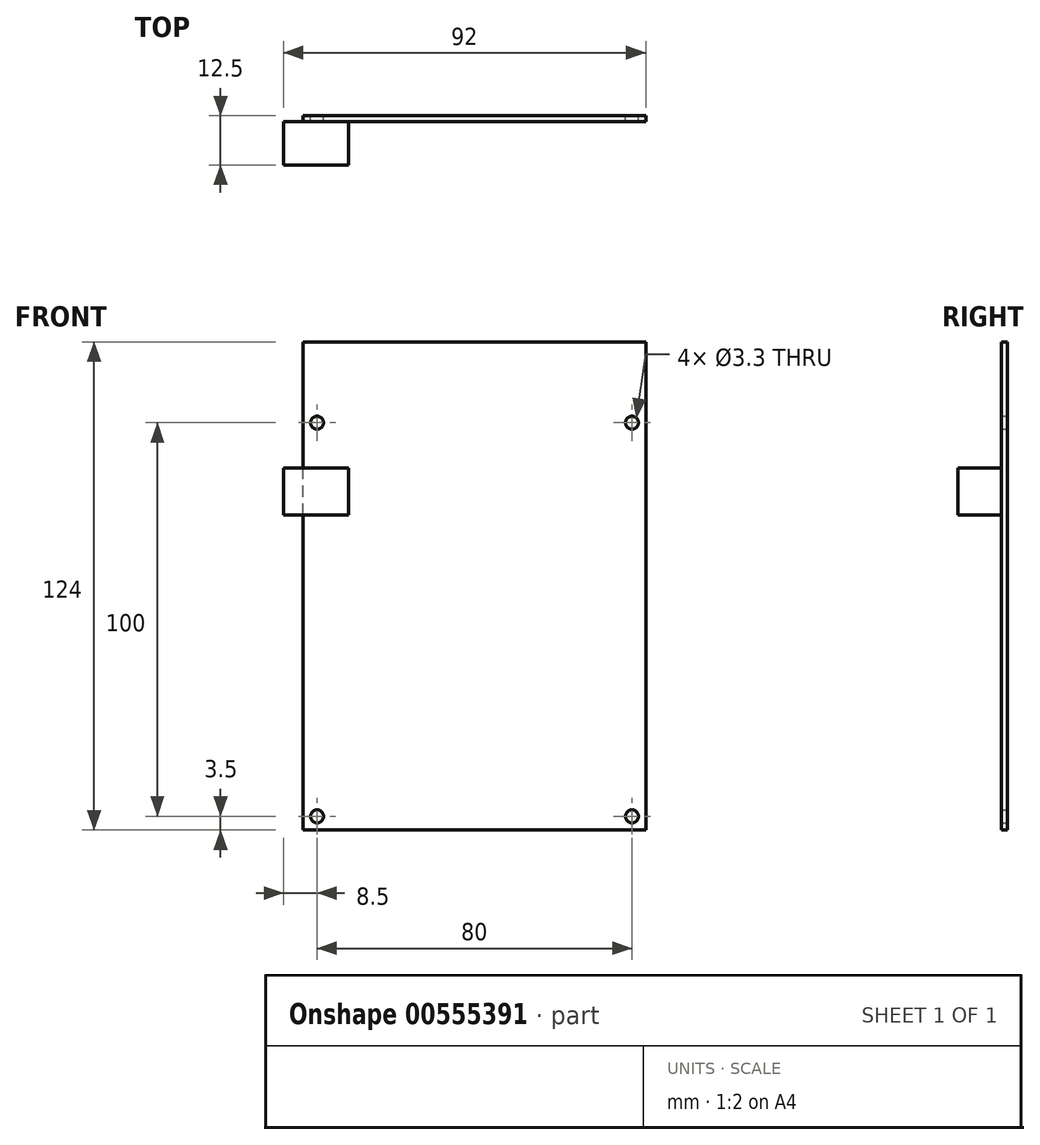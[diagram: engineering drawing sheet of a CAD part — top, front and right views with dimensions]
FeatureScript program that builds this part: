
annotation { "Feature Type Name" : "Feature", "Feature Type Description" : "" }
export const myFeature = defineFeature(function(context is Context, id is Id, definition is map)
    precondition{}
    {
        {
            var Q0;
            Q0=qCreatedBy(makeId("Front.planeOp"),FACE);
            var sketch = newSketch(context, id + "F0", { "sketchPlane" : qUnion([Q0])});
            skLineSegment(sketch, "E0.bottom", {"start": v(43.5, -62) * mm, "end": v(-43.5, -62) * mm});
            skLineSegment(sketch, "E0.top", {"start": v(43.5, 62) * mm, "end": v(-43.5, 62) * mm});
            skLineSegment(sketch, "E0.left", {"start": v(43.5, -62) * mm, "end": v(43.5, 62) * mm});
            skLineSegment(sketch, "E0.right", {"start": v(-43.5, -62) * mm, "end": v(-43.5, 62) * mm});
            skPoint(sketch, "E0.middle", {"position": v(0, 0) * mm});
            skCircle(sketch, "E1", {"center": v(-40, 41.5) * mm, "radius": 1.65 * mm});
            skCircle(sketch, "E2", {"center": v(-40, -58.5) * mm, "radius": 1.65 * mm});
            skCircle(sketch, "E3", {"center": v(40, 41.5) * mm, "radius": 1.65 * mm});
            skCircle(sketch, "E4", {"center": v(40, -58.5) * mm, "radius": 1.65 * mm});
            skLineSegment(sketch, "E5", {"start": v(0, 62) * mm, "end": v(0, -62) * mm, "construction": true});
            skSolve(sketch);
        }
        {
            var Q0;
            Q0=makeQuery(id+"F0.imprint","IMPRINT",FACE,{"disambiguationData":[TD([[makeQuery(id+"F0.imprint","IMPRINT",EDGE,{"derivedFrom":sQuery(id+"F0.wireOp",EDGE,"E0.bottom")}),-1.0]])]});
            extrude(context, id + "F1", {"entities" : qUnion([Q0]), "depth" : 1.5 * mm, "offsetDistance" : 25 * mm});
        }
        {
            var Q0;
            Q0=makeQuery(id+"F1.opExtrude","CAP_FACE",FACE,{"disambiguationData":[OSD([sQuery(id+"F0.wireOp",EDGE,"E0.bottom"),sQuery(id+"F0.wireOp",EDGE,"E0.top"),sQuery(id+"F0.wireOp",EDGE,"E0.left"),sQuery(id+"F0.wireOp",EDGE,"E0.right"),sQuery(id+"F0.wireOp",EDGE,"E1"),sQuery(id+"F0.wireOp",EDGE,"E2"),sQuery(id+"F0.wireOp",EDGE,"E3"),sQuery(id+"F0.wireOp",EDGE,"E4")])],"isStart":false});
            var sketch = newSketch(context, id + "F2", { "sketchPlane" : qUnion([Q0])});
            skLineSegment(sketch, "E6.bottom", {"start": v(-32, 30) * mm, "end": v(-48.5, 30) * mm});
            skLineSegment(sketch, "E6.top", {"start": v(-32, 18) * mm, "end": v(-48.5, 18) * mm});
            skLineSegment(sketch, "E6.left", {"start": v(-32, 30) * mm, "end": v(-32, 18) * mm});
            skLineSegment(sketch, "E6.right", {"start": v(-48.5, 30) * mm, "end": v(-48.5, 18) * mm});
            skSolve(sketch);
        }
        {
            var Q0;
            {var subQ0=sQuery(id+"F2.wireOp",EDGE,"E6.right");Q0=makeQuery(id+"F2.imprint","IMPRINT",FACE,{"disambiguationData":[TD([[makeQuery(id+"F2.imprint","IMPRINT",EDGE,{"derivedFrom":subQ0}),1.0]])]});}
            var Q1;
            {var subQ0=sQuery(id+"F2.wireOp",EDGE,"E6.left");Q1=makeQuery(id+"F2.imprint","IMPRINT",FACE,{"disambiguationData":[TD([[makeQuery(id+"F2.imprint","IMPRINT",EDGE,{"derivedFrom":subQ0}),-1.0]])]});}
            extrude(context, id + "F3", {"entities" : qUnion([Q0, Q1]), "operationType" : NewBodyOperationType.ADD, "depth" : 11 * mm, "offsetDistance" : 25 * mm});
        }
    });
